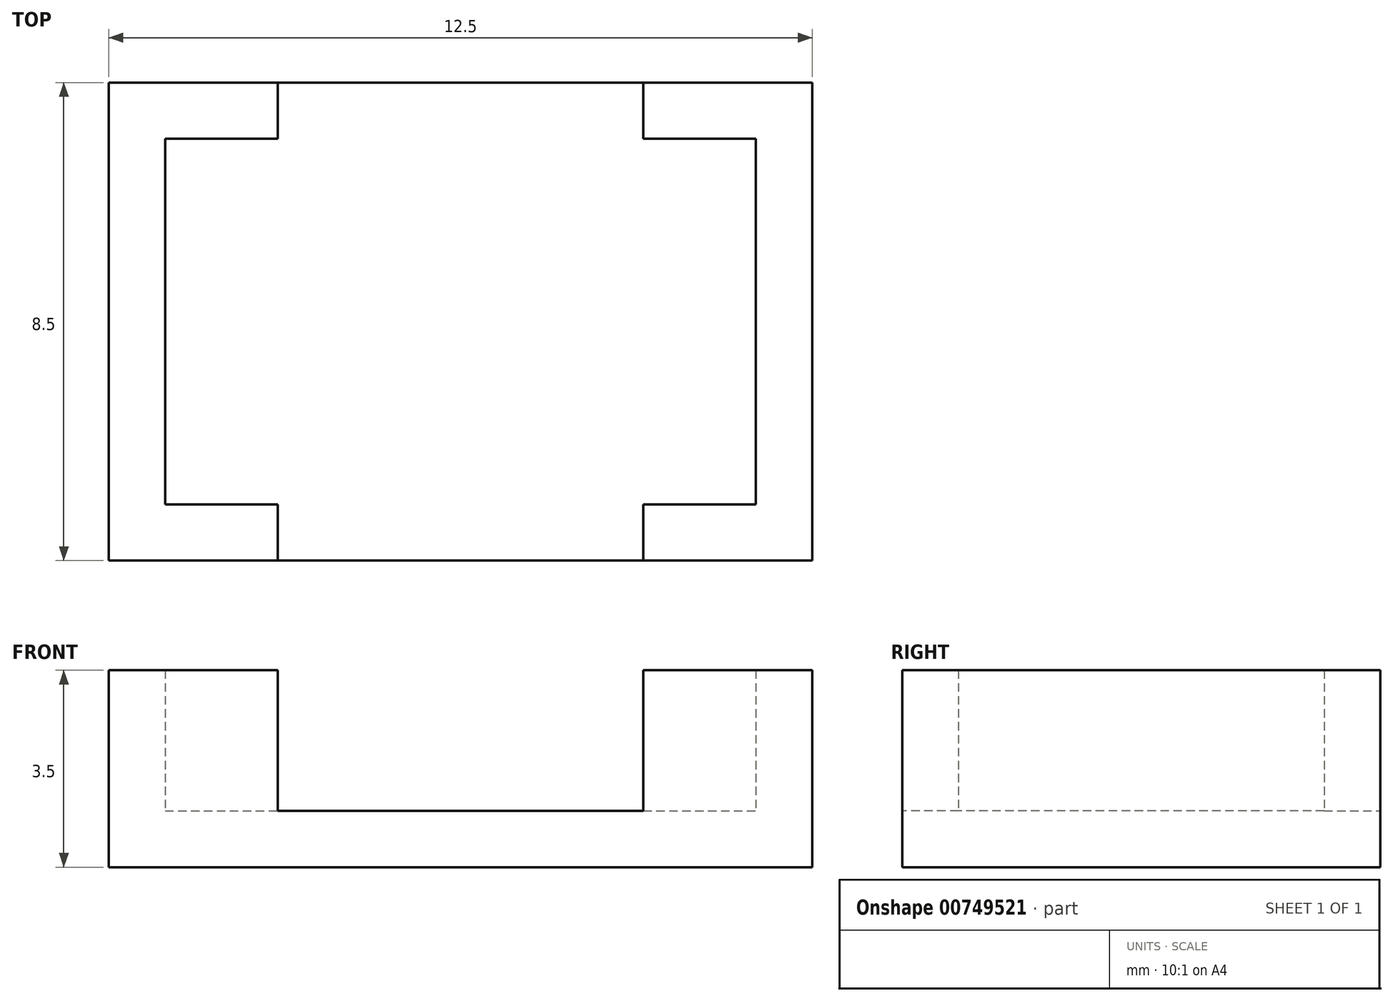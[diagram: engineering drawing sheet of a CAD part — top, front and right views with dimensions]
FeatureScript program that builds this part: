
annotation { "Feature Type Name" : "Feature", "Feature Type Description" : "" }
export const myFeature = defineFeature(function(context is Context, id is Id, definition is map)
    precondition{}
    {
        {
            var Q0;
            Q0=qCreatedBy(makeId("Top.planeOp"),FACE);
            var sketch = newSketch(context, id + "F0", { "sketchPlane" : qUnion([Q0])});
            skLineSegment(sketch, "E0.bottom", {"start": v(-6.25, 4.25) * mm, "end": v(6.25, 4.25) * mm});
            skLineSegment(sketch, "E0.top", {"start": v(-6.25, -4.25) * mm, "end": v(6.25, -4.25) * mm});
            skLineSegment(sketch, "E0.left", {"start": v(-6.25, 4.25) * mm, "end": v(-6.25, -4.25) * mm});
            skLineSegment(sketch, "E0.right", {"start": v(6.25, 4.25) * mm, "end": v(6.25, -4.25) * mm});
            skSolve(sketch);
        }
        {
            var Q0;
            Q0=makeQuery(id+"F0.imprint","IMPRINT",FACE,{"disambiguationData":[TD([[makeQuery(id+"F0.imprint","IMPRINT",EDGE,{"derivedFrom":sQuery(id+"F0.wireOp",EDGE,"E0.bottom")}),-1.0]])]});
            extrude(context, id + "F1", {"entities" : qUnion([Q0]), "depth" : 1 * mm, "offsetDistance" : 25 * mm});
        }
        {
            var Q0;
            Q0=makeQuery(id+"F1.opExtrude","CAP_FACE",FACE,{"disambiguationData":[OSD([sQuery(id+"F0.wireOp",EDGE,"E0.bottom"),sQuery(id+"F0.wireOp",EDGE,"E0.top"),sQuery(id+"F0.wireOp",EDGE,"E0.left"),sQuery(id+"F0.wireOp",EDGE,"E0.right")])],"isStart":false});
            var sketch = newSketch(context, id + "F2", { "sketchPlane" : qUnion([Q0])});
            skLineSegment(sketch, "E1.bottom", {"start": v(-5.25, 3.25) * mm, "end": v(5.25, 3.25) * mm});
            skLineSegment(sketch, "E1.top", {"start": v(-5.25, -3.25) * mm, "end": v(5.25, -3.25) * mm});
            skLineSegment(sketch, "E1.left", {"start": v(-5.25, 3.25) * mm, "end": v(-5.25, -3.25) * mm});
            skLineSegment(sketch, "E2", {"start": v(5.25, -3.25) * mm, "end": v(5.25, 3.25) * mm});
            skLineSegment(sketch, "E3", {"start": v(-3.25, 3.25) * mm, "end": v(-3.25, 4.25) * mm});
            skLineSegment(sketch, "E4", {"start": v(3.25, 3.25) * mm, "end": v(3.25, 4.25) * mm});
            skLineSegment(sketch, "E5", {"start": v(-3.25, -3.25) * mm, "end": v(-3.25, -4.25) * mm});
            skLineSegment(sketch, "E6", {"start": v(3.25, -3.25) * mm, "end": v(3.25, -4.25) * mm});
            skSolve(sketch);
        }
        {
            var Q0;
            {var subQ0=sQuery(id+"F2.wireOp",EDGE,"E1.left");Q0=makeQuery(id+"F2.imprint","IMPRINT",FACE,{"disambiguationData":[TD([[makeQuery(id+"F2.imprint","IMPRINT",EDGE,{"derivedFrom":subQ0}),-1.0]])]});}
            var Q1;
            {var subQ1=sQuery(id+"F2.wireOp",EDGE,"E2");Q1=makeQuery(id+"F2.imprint","IMPRINT",FACE,{"disambiguationData":[TD([[makeQuery(id+"F2.imprint","IMPRINT",EDGE,{"derivedFrom":subQ1}),-1.0]])]});}
            extrude(context, id + "F3", {"entities" : qUnion([Q0, Q1]), "operationType" : NewBodyOperationType.ADD, "depth" : 2.5 * mm, "offsetDistance" : 25 * mm});
        }
    });
